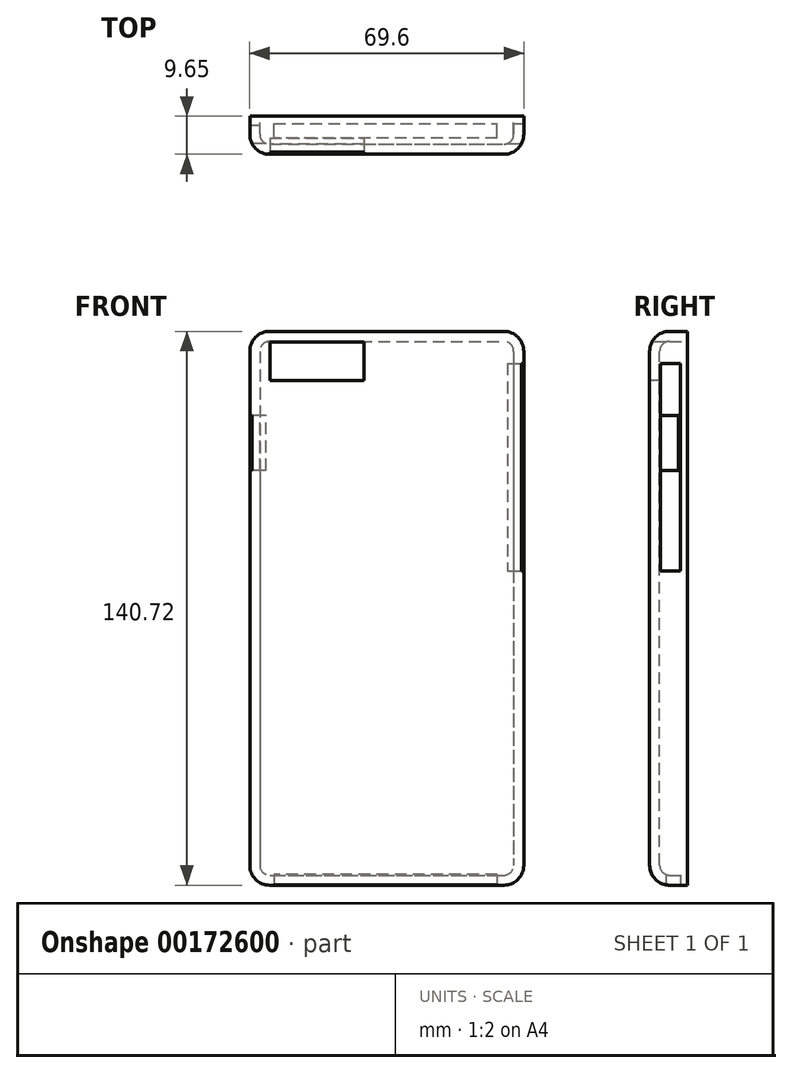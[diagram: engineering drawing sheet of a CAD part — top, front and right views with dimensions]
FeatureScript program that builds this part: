
annotation { "Feature Type Name" : "Feature", "Feature Type Description" : "" }
export const myFeature = defineFeature(function(context is Context, id is Id, definition is map)
    precondition{}
    {
        {
            var Q0;
            Q0=qCreatedBy(makeId("Front.planeOp"),FACE);
            var sketch = newSketch(context, id + "F0", { "sketchPlane" : qUnion([Q0])});
            skLineSegment(sketch, "E0.bottom", {"start": v(-34.8, 70.36) * mm, "end": v(34.8, 70.36) * mm});
            skLineSegment(sketch, "E0.top", {"start": v(-34.8, -70.36) * mm, "end": v(34.8, -70.36) * mm});
            skLineSegment(sketch, "E0.left", {"start": v(-34.8, 70.36) * mm, "end": v(-34.8, -70.36) * mm});
            skLineSegment(sketch, "E0.right", {"start": v(34.8, 70.36) * mm, "end": v(34.8, -70.36) * mm});
            skPoint(sketch, "E0.middle", {"position": v(0, 0) * mm});
            skSolve(sketch);
        }
        {
            var Q0;
            Q0 = qSketchRegion(id + "F0", true);
            extrude(context, id + "F1", {"entities" : qUnion([Q0]), "depth" : 9.65 * mm});
        }
        {
            var Q0;
            Q0=makeQuery(id+"F1.opExtrude","SWEPT_EDGE",EDGE,{"disambiguationData":[OSD([sQuery(id+"F0.wireOp",EDGE,"E0.bottom"),sQuery(id+"F0.wireOp",EDGE,"E0.left")])]});
            var Q1;
            Q1=makeQuery(id+"F1.opExtrude","CAP_EDGE",EDGE,{"disambiguationData":[OSD([sQuery(id+"F0.wireOp",EDGE,"E0.bottom")])],"isStart":false});
            var Q2;
            Q2=makeQuery(id+"F1.opExtrude","CAP_FACE",FACE,{"disambiguationData":[OSD([sQuery(id+"F0.wireOp",EDGE,"E0.bottom"),sQuery(id+"F0.wireOp",EDGE,"E0.top"),sQuery(id+"F0.wireOp",EDGE,"E0.left"),sQuery(id+"F0.wireOp",EDGE,"E0.right")])],"isStart":false});
            var Q3;
            Q3=makeQuery(id+"F1.opExtrude","CAP_EDGE",EDGE,{"disambiguationData":[OSD([sQuery(id+"F0.wireOp",EDGE,"E0.top")])],"isStart":false});
            fillet(context, id + "F2", {"entities" : qUnion([Q0, Q1, Q2, Q3]), "radius" : 5.08 * mm, "tangentPropagation" : true, "allowEdgeOverflow" : false});
        }
        {
            var Q0;
            Q0=makeQuery(id+"F2.opFillet","BLEND_EDGE",EDGE,{"blendedFrom":[makeQuery(id+"F1.opExtrude","CAP_EDGE",EDGE,{"disambiguationData":[OSD([sQuery(id+"F0.wireOp",EDGE,"E0.bottom")])],"isStart":false}),makeQuery(id+"F1.opExtrude","CAP_EDGE",EDGE,{"disambiguationData":[OSD([sQuery(id+"F0.wireOp",EDGE,"E0.right")])],"isStart":false})],"blendedInto":[]});
            fillet(context, id + "F3", {"entities" : qUnion([Q0]), "radius" : 5.08 * mm, "tangentPropagation" : true, "allowEdgeOverflow" : false});
        }
        {
            var Q0;
            Q0=makeQuery(id+"F2.opFillet","BLEND_EDGE",EDGE,{"blendedFrom":[makeQuery(id+"F1.opExtrude","CAP_EDGE",EDGE,{"disambiguationData":[OSD([sQuery(id+"F0.wireOp",EDGE,"E0.top")])],"isStart":false}),makeQuery(id+"F1.opExtrude","CAP_EDGE",EDGE,{"disambiguationData":[OSD([sQuery(id+"F0.wireOp",EDGE,"E0.left")])],"isStart":false})],"blendedInto":[]});
            fillet(context, id + "F4", {"entities" : qUnion([Q0]), "radius" : 5.08 * mm, "tangentPropagation" : true, "allowEdgeOverflow" : false});
        }
        {
            var Q0;
            Q0=makeQuery(id+"F2.opFillet","BLEND_EDGE",EDGE,{"blendedFrom":[makeQuery(id+"F1.opExtrude","CAP_EDGE",EDGE,{"disambiguationData":[OSD([sQuery(id+"F0.wireOp",EDGE,"E0.top")])],"isStart":false}),makeQuery(id+"F1.opExtrude","CAP_EDGE",EDGE,{"disambiguationData":[OSD([sQuery(id+"F0.wireOp",EDGE,"E0.right")])],"isStart":false})],"blendedInto":[]});
            fillet(context, id + "F5", {"entities" : qUnion([Q0]), "radius" : 5.08 * mm, "tangentPropagation" : true, "allowEdgeOverflow" : false});
        }
        {
            var Q0;
            Q0=makeQuery(id+"F1.opExtrude","CAP_FACE",FACE,{"disambiguationData":[OSD([sQuery(id+"F0.wireOp",EDGE,"E0.bottom"),sQuery(id+"F0.wireOp",EDGE,"E0.top"),sQuery(id+"F0.wireOp",EDGE,"E0.left"),sQuery(id+"F0.wireOp",EDGE,"E0.right")])],"isStart":true});
            shell(context, id + "F6", {"entities" : qUnion([Q0]), "thickness" : 2.54 * mm});
        }
        {
            var Q0;
            Q0=makeQuery(id+"F1.opExtrude","CAP_FACE",FACE,{"disambiguationData":[OSD([sQuery(id+"F0.wireOp",EDGE,"E0.bottom"),sQuery(id+"F0.wireOp",EDGE,"E0.top"),sQuery(id+"F0.wireOp",EDGE,"E0.left"),sQuery(id+"F0.wireOp",EDGE,"E0.right")])],"isStart":false});
            var sketch = newSketch(context, id + "F7", { "sketchPlane" : qUnion([Q0])});
            skLineSegment(sketch, "E1.bottom", {"start": v(-5.77, 57.93) * mm, "end": v(-29.72, 57.93) * mm});
            skLineSegment(sketch, "E1.top", {"start": v(-5.77, 67.65) * mm, "end": v(-29.72, 67.65) * mm});
            skLineSegment(sketch, "E1.left", {"start": v(-5.77, 57.93) * mm, "end": v(-5.77, 67.65) * mm});
            skLineSegment(sketch, "E1.right", {"start": v(-29.72, 57.93) * mm, "end": v(-29.72, 67.65) * mm});
            skSolve(sketch);
        }
        {
            var Q0;
            Q0 = qSketchRegion(id + "F7", true);
            extrude(context, id + "F8", {"entities" : qUnion([Q0]), "operationType" : NewBodyOperationType.REMOVE, "oppositeDirection" : true, "depth" : 25.4 * mm});
        }
        {
            var Q0;
            Q0=makeQuery(id+"F1.opExtrude","SWEPT_FACE",FACE,{"disambiguationData":[OSD([sQuery(id+"F0.wireOp",EDGE,"E0.right")])]});
            var sketch = newSketch(context, id + "F9", { "sketchPlane" : qUnion([Q0])});
            skLineSegment(sketch, "E2.bottom", {"start": v(-1.81, 62.21) * mm, "end": v(-6.92, 62.21) * mm});
            skLineSegment(sketch, "E2.top", {"start": v(-1.81, 9.48) * mm, "end": v(-6.92, 9.48) * mm});
            skLineSegment(sketch, "E2.left", {"start": v(-1.81, 62.21) * mm, "end": v(-1.81, 9.48) * mm});
            skLineSegment(sketch, "E2.right", {"start": v(-6.92, 62.21) * mm, "end": v(-6.92, 9.48) * mm});
            skSolve(sketch);
        }
        {
            var Q0;
            Q0 = qSketchRegion(id + "F9", true);
            extrude(context, id + "F10", {"entities" : qUnion([Q0]), "operationType" : NewBodyOperationType.REMOVE, "oppositeDirection" : true, "depth" : 25.4 * mm});
        }
        {
            var Q0;
            Q0=makeQuery(id+"F1.opExtrude","SWEPT_FACE",FACE,{"disambiguationData":[OSD([sQuery(id+"F0.wireOp",EDGE,"E0.left")])]});
            var sketch = newSketch(context, id + "F11", { "sketchPlane" : qUnion([Q0])});
            skLineSegment(sketch, "E3.bottom", {"start": v(2.3, 49.03) * mm, "end": v(6.92, 49.03) * mm});
            skLineSegment(sketch, "E3.top", {"start": v(2.3, 35.02) * mm, "end": v(6.92, 35.02) * mm});
            skLineSegment(sketch, "E3.left", {"start": v(2.3, 49.03) * mm, "end": v(2.3, 35.02) * mm});
            skLineSegment(sketch, "E3.right", {"start": v(6.92, 49.03) * mm, "end": v(6.92, 35.02) * mm});
            skSolve(sketch);
        }
        {
            var Q0;
            Q0 = qSketchRegion(id + "F11", true);
            extrude(context, id + "F12", {"entities" : qUnion([Q0]), "operationType" : NewBodyOperationType.REMOVE, "oppositeDirection" : true, "depth" : 25.4 * mm});
        }
        {
            var Q0;
            Q0=makeQuery(id+"F1.opExtrude","SWEPT_FACE",FACE,{"disambiguationData":[OSD([sQuery(id+"F0.wireOp",EDGE,"E0.top")])]});
            var sketch = newSketch(context, id + "F13", { "sketchPlane" : qUnion([Q0])});
            skSolve(sketch);
        }
        {
            var Q0;
            {var subQ0=sQuery(id+"F0.wireOp",EDGE,"E0.top");Q0=makeQuery(id+"F13.imprint","IMPRINT",FACE,{"disambiguationData":[TD([[makeQuery(id+"F13.imprint","IMPRINT",EDGE,{"derivedFrom":makeQuery(id+"F1.opExtrude","CAP_EDGE",EDGE,{"disambiguationData":[OSD([subQ0])],"isStart":true})}),1.0]])]});}
            var sketch = newSketch(context, id + "F14", { "sketchPlane" : qUnion([Q0])});
            skLineSegment(sketch, "E4.bottom", {"start": v(28.03, 1.88) * mm, "end": v(-28.66, 1.88) * mm});
            skLineSegment(sketch, "E4.top", {"start": v(28.03, 5.5) * mm, "end": v(-28.66, 5.5) * mm});
            skLineSegment(sketch, "E4.left", {"start": v(28.03, 1.88) * mm, "end": v(28.03, 5.5) * mm});
            skLineSegment(sketch, "E4.right", {"start": v(-28.66, 1.88) * mm, "end": v(-28.66, 5.5) * mm});
            skSolve(sketch);
        }
        {
            var Q0;
            Q0 = qSketchRegion(id + "F14", true);
            extrude(context, id + "F15", {"entities" : qUnion([Q0]), "operationType" : NewBodyOperationType.REMOVE, "oppositeDirection" : true, "depth" : 25.4 * mm});
        }
    });
